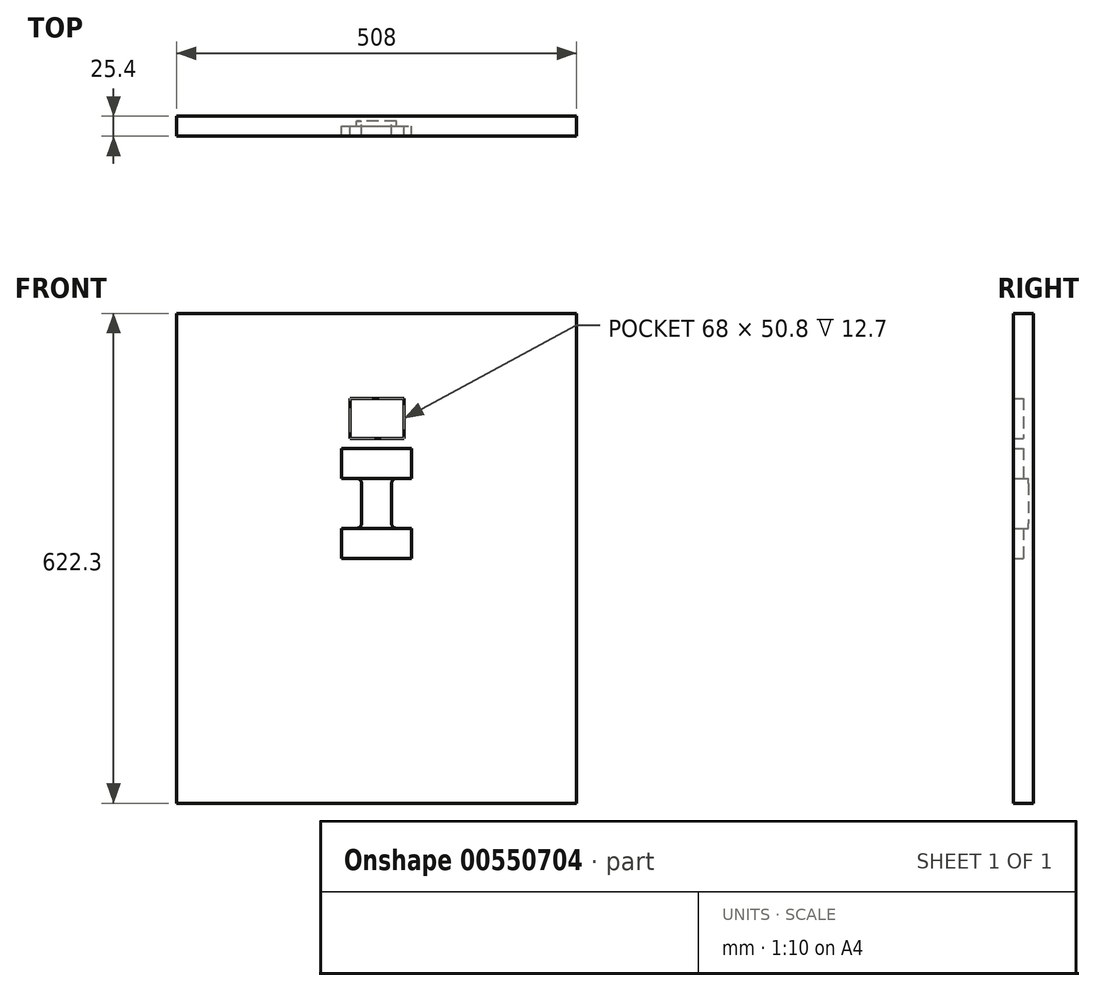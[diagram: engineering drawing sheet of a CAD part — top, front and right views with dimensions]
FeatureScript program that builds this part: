
annotation { "Feature Type Name" : "Feature", "Feature Type Description" : "" }
export const myFeature = defineFeature(function(context is Context, id is Id, definition is map)
    precondition{}
    {
        {
            var Q0;
            Q0=qCreatedBy(makeId("Front.planeOp"),FACE);
            var sketch = newSketch(context, id + "F0", { "sketchPlane" : qUnion([Q0])});
            skLineSegment(sketch, "E0.bottom", {"start": v(-254, 308.97) * mm, "end": v(254, 308.97) * mm});
            skLineSegment(sketch, "E0.top", {"start": v(-254, -313.33) * mm, "end": v(254, -313.33) * mm});
            skLineSegment(sketch, "E0.left", {"start": v(-254, 308.97) * mm, "end": v(-254, -313.33) * mm});
            skLineSegment(sketch, "E0.right", {"start": v(254, 308.97) * mm, "end": v(254, -313.33) * mm});
            skLineSegment(sketch, "E1.bottom", {"start": v(-33.42, 201.02) * mm, "end": v(34.58, 201.02) * mm});
            skLineSegment(sketch, "E1.top", {"start": v(-33.42, 150.22) * mm, "end": v(34.58, 150.22) * mm});
            skLineSegment(sketch, "E1.left", {"start": v(-33.42, 201.02) * mm, "end": v(-33.42, 150.22) * mm});
            skLineSegment(sketch, "E1.right", {"start": v(34.58, 201.02) * mm, "end": v(34.58, 150.22) * mm});
            skLineSegment(sketch, "E2", {"start": v(-63.5, -18.05) * mm, "end": v(63.5, -18.05) * mm, "construction": true});
            skLineSegment(sketch, "E3.bottom", {"start": v(-44.45, 137.52) * mm, "end": v(44.45, 137.52) * mm});
            skLineSegment(sketch, "E3.top", {"start": v(-44.45, 99.42) * mm, "end": v(-25.4, 99.42) * mm});
            skLineSegment(sketch, "E3.left", {"start": v(-44.45, 137.52) * mm, "end": v(-44.45, 99.42) * mm});
            skLineSegment(sketch, "E3.right", {"start": v(44.45, 137.52) * mm, "end": v(44.45, 99.42) * mm});
            skLineSegment(sketch, "E4.bottom", {"start": v(-44.45, 35.92) * mm, "end": v(-25.4, 35.92) * mm});
            skLineSegment(sketch, "E4.top", {"start": v(-44.45, -2.18) * mm, "end": v(44.45, -2.18) * mm});
            skLineSegment(sketch, "E4.left", {"start": v(-44.45, 35.92) * mm, "end": v(-44.45, -2.18) * mm});
            skLineSegment(sketch, "E4.right", {"start": v(44.45, 35.92) * mm, "end": v(44.45, -2.18) * mm});
            skPoint(sketch, "E5", {"position": v(0, 137.52) * mm});
            skLineSegment(sketch, "E6.left", {"start": v(-19.05, 93.07) * mm, "end": v(-19.05, 42.27) * mm});
            skLineSegment(sketch, "E6.right", {"start": v(19.05, 93.07) * mm, "end": v(19.05, 42.27) * mm});
            skLineSegment(sketch, "E7.trimOffspring", {"start": v(25.4, 99.42) * mm, "end": v(44.45, 99.42) * mm});
            skLineSegment(sketch, "E8.trimOffspring", {"start": v(25.4, 35.92) * mm, "end": v(44.45, 35.92) * mm});
            skPoint(sketch, "E9.visualSharp", {"position": v(19.05, 99.42) * mm});
            skArc(sketch, "E9.filletArc", {"start": v(25.4, 99.42) * mm, "mid": v(20.9, 97.56) * mm, "end": v(19.05, 93.07) * mm});
            skPoint(sketch, "E10.visualSharp", {"position": v(19.05, 35.92) * mm});
            skArc(sketch, "E10.filletArc", {"start": v(19.05, 42.27) * mm, "mid": v(20.9, 37.78) * mm, "end": v(25.4, 35.92) * mm});
            skPoint(sketch, "E11.visualSharp", {"position": v(-19.05, 35.92) * mm});
            skArc(sketch, "E11.filletArc", {"start": v(-25.4, 35.92) * mm, "mid": v(-20.9, 37.78) * mm, "end": v(-19.05, 42.27) * mm});
            skPoint(sketch, "E12.visualSharp", {"position": v(-19.05, 99.42) * mm});
            skArc(sketch, "E12.filletArc", {"start": v(-19.05, 93.07) * mm, "mid": v(-20.9, 97.56) * mm, "end": v(-25.4, 99.42) * mm});
            skLineSegment(sketch, "E13", {"start": v(-25.4, 99.42) * mm, "end": v(25.4, 99.42) * mm});
            skLineSegment(sketch, "E14", {"start": v(25.4, 35.92) * mm, "end": v(-25.4, 35.92) * mm});
            skSolve(sketch);
        }
        {
            var Q0;
            Q0=makeQuery(id+"F0.imprint","IMPRINT",FACE,{"disambiguationData":[TD([[makeQuery(id+"F0.imprint","IMPRINT",EDGE,{"derivedFrom":sQuery(id+"F0.wireOp",EDGE,"E0.bottom")}),-1.0]])]});
            extrude(context, id + "F1", {"entities" : qUnion([Q0]), "depth" : 25.4 * mm, "offsetDistance" : 25.4 * mm});
        }
        {
            var Q0;
            Q0=makeQuery(id+"F0.imprint","IMPRINT",FACE,{"disambiguationData":[TD([[makeQuery(id+"F0.imprint","IMPRINT",EDGE,{"derivedFrom":sQuery(id+"F0.wireOp",EDGE,"E1.bottom")}),-1.0]])]});
            var Q1;
            Q1=makeQuery(id+"F0.imprint","IMPRINT",FACE,{"disambiguationData":[TD([[makeQuery(id+"F0.imprint","IMPRINT",EDGE,{"derivedFrom":sQuery(id+"F0.wireOp",EDGE,"E3.bottom")}),-1.0]])]});
            var Q2;
            Q2=makeQuery(id+"F0.imprint","IMPRINT",FACE,{"disambiguationData":[TD([[makeQuery(id+"F0.imprint","IMPRINT",EDGE,{"derivedFrom":sQuery(id+"F0.wireOp",EDGE,"E4.bottom")}),-1.0]])]});
            extrude(context, id + "F2", {"entities" : qUnion([Q0, Q1, Q2]), "operationType" : NewBodyOperationType.ADD, "depth" : 12.7 * mm, "offsetDistance" : 25.4 * mm});
        }
        {
            var Q0;
            Q0=makeQuery(id+"F0.imprint","IMPRINT",FACE,{"disambiguationData":[TD([[makeQuery(id+"F0.imprint","IMPRINT",EDGE,{"derivedFrom":sQuery(id+"F0.wireOp",EDGE,"E6.left")}),1.0]])]});
            extrude(context, id + "F3", {"entities" : qUnion([Q0]), "operationType" : NewBodyOperationType.ADD, "depth" : 6.35 * mm, "offsetDistance" : 25.4 * mm});
        }
    });
